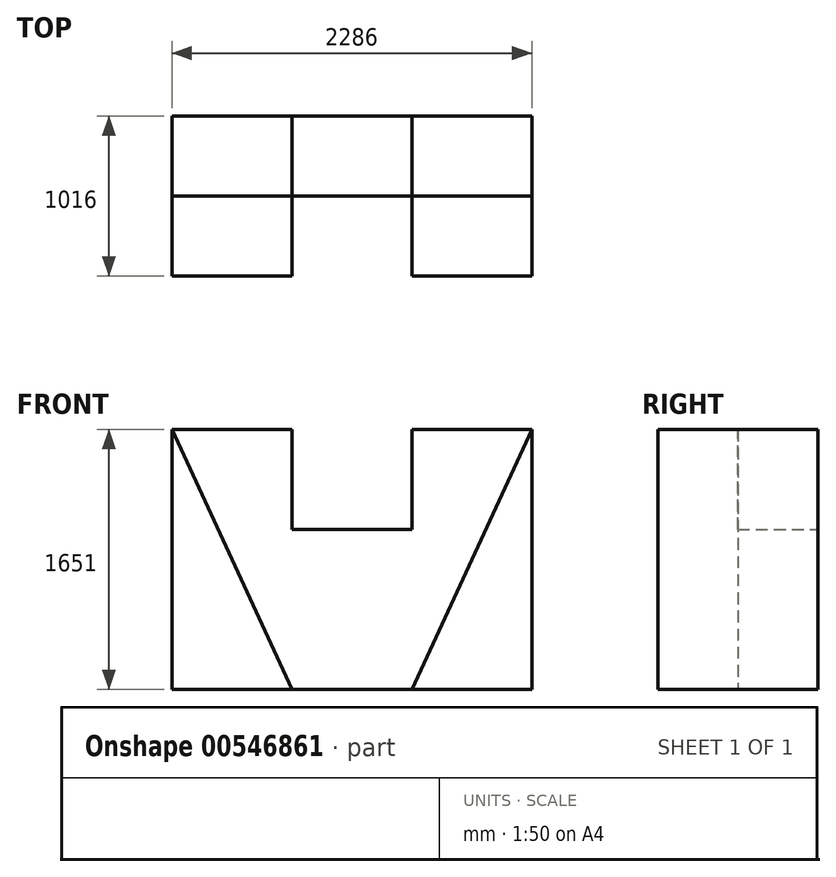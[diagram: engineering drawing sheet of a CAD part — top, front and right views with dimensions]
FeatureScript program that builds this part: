
annotation { "Feature Type Name" : "Feature", "Feature Type Description" : "" }
export const myFeature = defineFeature(function(context is Context, id is Id, definition is map)
    precondition{}
    {
        {
            var Q0;
            Q0=qCreatedBy(makeId("Front.planeOp"),FACE);
            var sketch = newSketch(context, id + "F0", { "sketchPlane" : qUnion([Q0])});
            skLineSegment(sketch, "E0.bottom", {"start": v(1143, -825.5) * mm, "end": v(-1143, -825.5) * mm});
            skLineSegment(sketch, "E0.top", {"start": v(1143, 825.5) * mm, "end": v(381, 825.5) * mm});
            skLineSegment(sketch, "E0.left", {"start": v(1143, -825.5) * mm, "end": v(1143, 825.5) * mm});
            skLineSegment(sketch, "E0.right", {"start": v(-1143, -825.5) * mm, "end": v(-1143, 825.5) * mm});
            skPoint(sketch, "E0.middle", {"position": v(0, 0) * mm});
            skLineSegment(sketch, "E1", {"start": v(-381, -825.5) * mm, "end": v(-1143, -825.5) * mm});
            skLineSegment(sketch, "E2", {"start": v(381, -825.5) * mm, "end": v(1143, -825.5) * mm});
            skLineSegment(sketch, "E3.bottom", {"start": v(381, 190.5) * mm, "end": v(-381, 190.5) * mm});
            skLineSegment(sketch, "E3.left", {"start": v(381, 190.5) * mm, "end": v(381, 825.5) * mm});
            skLineSegment(sketch, "E3.right", {"start": v(-381, 190.5) * mm, "end": v(-381, 825.5) * mm});
            skLineSegment(sketch, "E4.trimOffspring", {"start": v(-381, 825.5) * mm, "end": v(-1143, 825.5) * mm});
            skSolve(sketch);
        }
        {
            var Q0;
            Q0=makeQuery(id+"F0.imprint","IMPRINT",FACE,{"disambiguationData":[TD([[makeQuery(id+"F0.imprint","IMPRINT",EDGE,{"derivedFrom":sQuery(id+"F0.wireOp",EDGE,"E0.bottom")}),-1.0]])]});
            extrude(context, id + "F1", {"entities" : qUnion([Q0]), "depth" : 508 * mm, "offsetDistance" : 25.4 * mm});
        }
        {
            var Q0;
            Q0=makeQuery(id+"F1.opExtrude","CAP_FACE",FACE,{"disambiguationData":[OSD([sQuery(id+"F0.wireOp",EDGE,"E0.bottom"),sQuery(id+"F0.wireOp",EDGE,"E0.top"),sQuery(id+"F0.wireOp",EDGE,"E0.left"),sQuery(id+"F0.wireOp",EDGE,"E0.right"),sQuery(id+"F0.wireOp",EDGE,"E1"),sQuery(id+"F0.wireOp",EDGE,"E2"),sQuery(id+"F0.wireOp",EDGE,"E3.bottom"),sQuery(id+"F0.wireOp",EDGE,"E3.left"),sQuery(id+"F0.wireOp",EDGE,"E3.right"),sQuery(id+"F0.wireOp",EDGE,"E4.trimOffspring")])],"isStart":false});
            var sketch = newSketch(context, id + "F2", { "sketchPlane" : qUnion([Q0])});
            skLineSegment(sketch, "E5", {"start": v(-1143, 825.5) * mm, "end": v(-381, -825.5) * mm});
            skLineSegment(sketch, "E6", {"start": v(-381, -825.5) * mm, "end": v(-1143, -825.5) * mm});
            skLineSegment(sketch, "E7", {"start": v(-1143, -825.5) * mm, "end": v(-1143, 825.5) * mm});
            skLineSegment(sketch, "E8", {"start": v(1143, 825.5) * mm, "end": v(381, -825.5) * mm});
            skLineSegment(sketch, "E9", {"start": v(381, -825.5) * mm, "end": v(1143, -825.5) * mm});
            skLineSegment(sketch, "E10", {"start": v(1143, -825.5) * mm, "end": v(1143, 825.5) * mm});
            skSolve(sketch);
        }
        {
            var Q0;
            Q0 = qSketchRegion(id + "F2", true);
            extrude(context, id + "F3", {"entities" : qUnion([Q0]), "operationType" : NewBodyOperationType.ADD, "depth" : 508 * mm, "offsetDistance" : 25.4 * mm});
        }
    });
